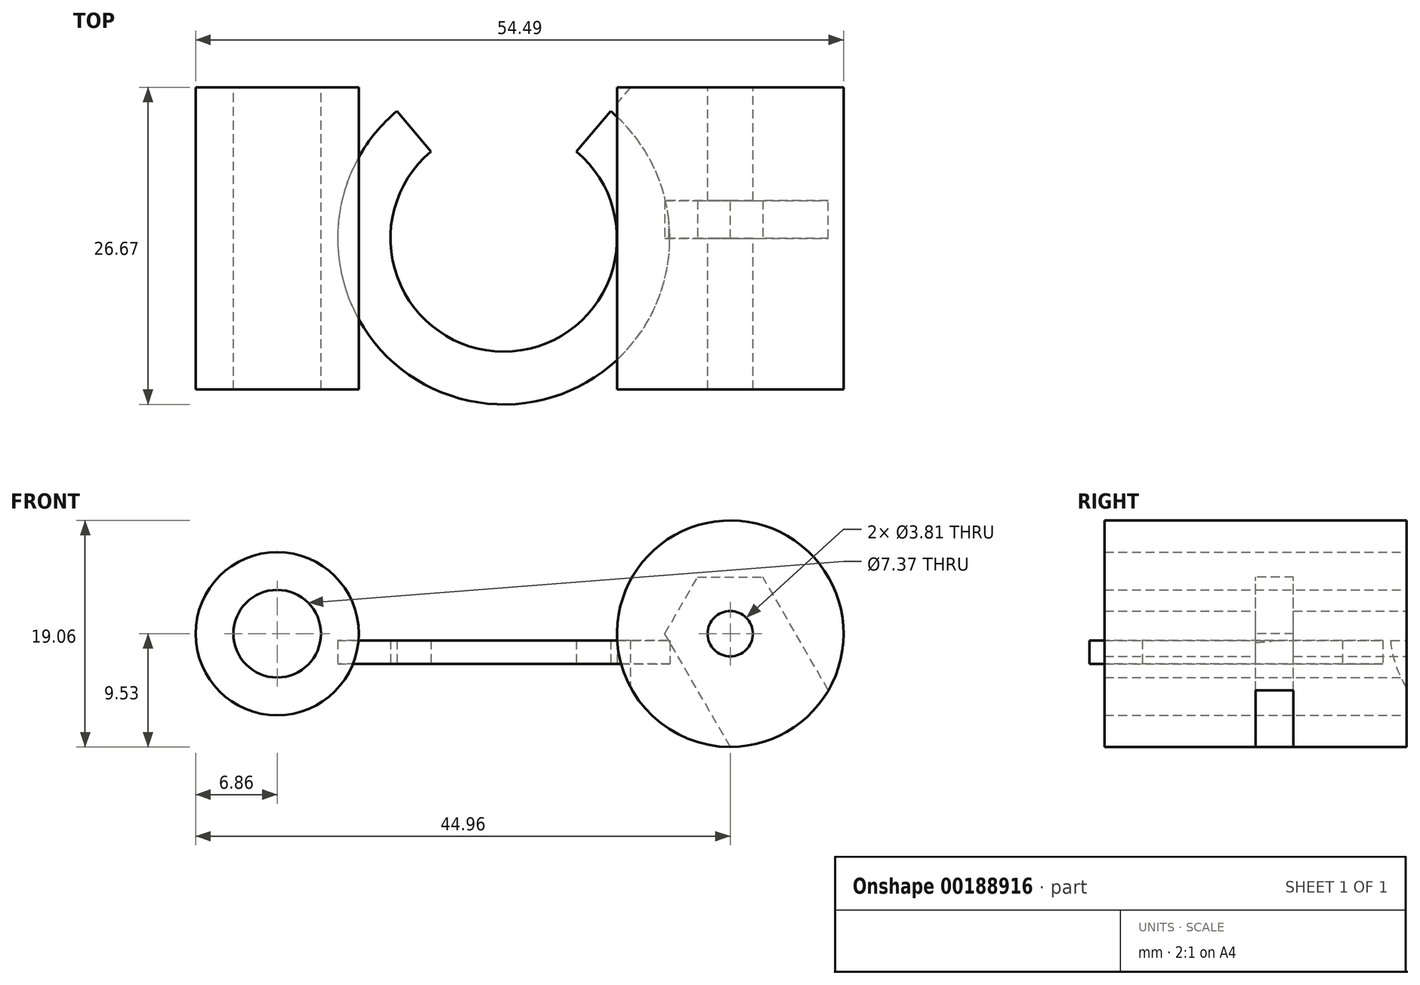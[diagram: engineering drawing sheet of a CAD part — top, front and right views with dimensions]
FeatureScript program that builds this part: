
annotation { "Feature Type Name" : "Feature", "Feature Type Description" : "" }
export const myFeature = defineFeature(function(context is Context, id is Id, definition is map)
    precondition{}
    {
        {
            var Q0;
            Q0=qCreatedBy(makeId("Front.planeOp"),FACE);
            var sketch = newSketch(context, id + "F0", { "sketchPlane" : qUnion([Q0])});
            skCircle(sketch, "E0", {"center": v(-19.05, 2.54) * mm, "radius": 3.68 * mm});
            skCircle(sketch, "E1", {"center": v(-19.05, 2.54) * mm, "radius": 6.86 * mm});
            skCircle(sketch, "E2", {"center": v(19.05, 2.54) * mm, "radius": 1.9 * mm});
            skLineSegment(sketch, "E3", {"start": v(-19.05, 2.54) * mm, "end": v(19.05, 2.54) * mm, "construction": true});
            skLineSegment(sketch, "E4", {"start": v(0, 2.54) * mm, "end": v(0, 0) * mm, "construction": true});
            skCircle(sketch, "E5", {"center": v(19.05, 2.54) * mm, "radius": 9.53 * mm});
            skSolve(sketch);
        }
        {
            var Q0;
            Q0=qSketchRegion(id+"F0",true);
            extrude(context, id + "F1", {"entities" : qUnion([Q0]), "endBound" : BoundingType.SYMMETRIC, "depth" : 25.4 * mm});
        }
        {
            var Q0;
            Q0=qCreatedBy(makeId("Top.planeOp"),FACE);
            var sketch = newSketch(context, id + "F2", { "sketchPlane" : qUnion([Q0])});
            skCircle(sketch, "E6", {"center": v(0, 0) * mm, "radius": 9.53 * mm});
            skCircle(sketch, "E7", {"center": v(0, 0) * mm, "radius": 13.97 * mm});
            skSolve(sketch);
        }
        {
            var Q0;
            Q0=qSketchRegion(id+"F2",true);
            extrude(context, id + "F3", {"entities" : qUnion([Q0]), "depth" : 1.98 * mm});
        }
        {
            var Q0;
            Q0=makeQuery(id+"F3.opExtrude","CAP_FACE",FACE,{"disambiguationData":[OSD([sQuery(id+"F2.wireOp",EDGE,"E6"),sQuery(id+"F2.wireOp",EDGE,"E7")])],"isStart":false});
            var sketch = newSketch(context, id + "F4", { "sketchPlane" : qUnion([Q0])});
            skLineSegment(sketch, "E8", {"start": v(0, 0) * mm, "end": v(-15.07, 17.96) * mm});
            skLineSegment(sketch, "E9", {"start": v(-15.07, 17.96) * mm, "end": v(15.07, 17.96) * mm});
            skLineSegment(sketch, "E10", {"start": v(15.07, 17.96) * mm, "end": v(0, 0) * mm});
            skLineSegment(sketch, "E11", {"start": v(0, 17.96) * mm, "end": v(0, 0) * mm, "construction": true});
            skSolve(sketch);
        }
        {
            var Q0;
            Q0=qSketchRegion(id+"F4",true);
            extrude(context, id + "F5", {"entities" : qUnion([Q0]), "operationType" : NewBodyOperationType.REMOVE, "oppositeDirection" : true, "depth" : 25.4 * mm});
        }
        {
            var Q0;
            Q0=qCreatedBy(makeId("Front.planeOp"),FACE);
            var sketch = newSketch(context, id + "F6", { "sketchPlane" : qUnion([Q0])});
            skCircle(sketch, "E12.cCircle", {"center": v(19.05, 2.54) * mm, "radius": 4.76 * mm, "construction": true});
            skLineSegment(sketch, "E12.0", {"start": v(16.3, 7.3) * mm, "end": v(21.8, 7.3) * mm});
            skLineSegment(sketch, "E12.1", {"start": v(21.8, 7.3) * mm, "end": v(24.55, 2.54) * mm});
            skLineSegment(sketch, "E12.4", {"start": v(16.3, -2.22) * mm, "end": v(13.55, 2.54) * mm});
            skLineSegment(sketch, "E12.5", {"start": v(13.55, 2.54) * mm, "end": v(16.3, 7.3) * mm});
            skPoint(sketch, "E12.0.midPoint", {"position": v(19.05, 7.3) * mm});
            skLineSegment(sketch, "E13", {"start": v(16.3, -2.22) * mm, "end": v(23.06, -13.93) * mm});
            skLineSegment(sketch, "E14", {"start": v(23.06, -13.93) * mm, "end": v(31.7, -9.84) * mm});
            skLineSegment(sketch, "E15", {"start": v(31.7, -9.84) * mm, "end": v(24.55, 2.54) * mm});
            skPoint(sketch, "E16.orphan", {"position": v(21.8, -2.22) * mm});
            skSolve(sketch);
        }
        {
            var Q0;
            Q0=qSketchRegion(id+"F6",true);
            extrude(context, id + "F7", {"entities" : qUnion([Q0]), "operationType" : NewBodyOperationType.REMOVE, "oppositeDirection" : true, "depth" : 3.17 * mm});
        }
    });
